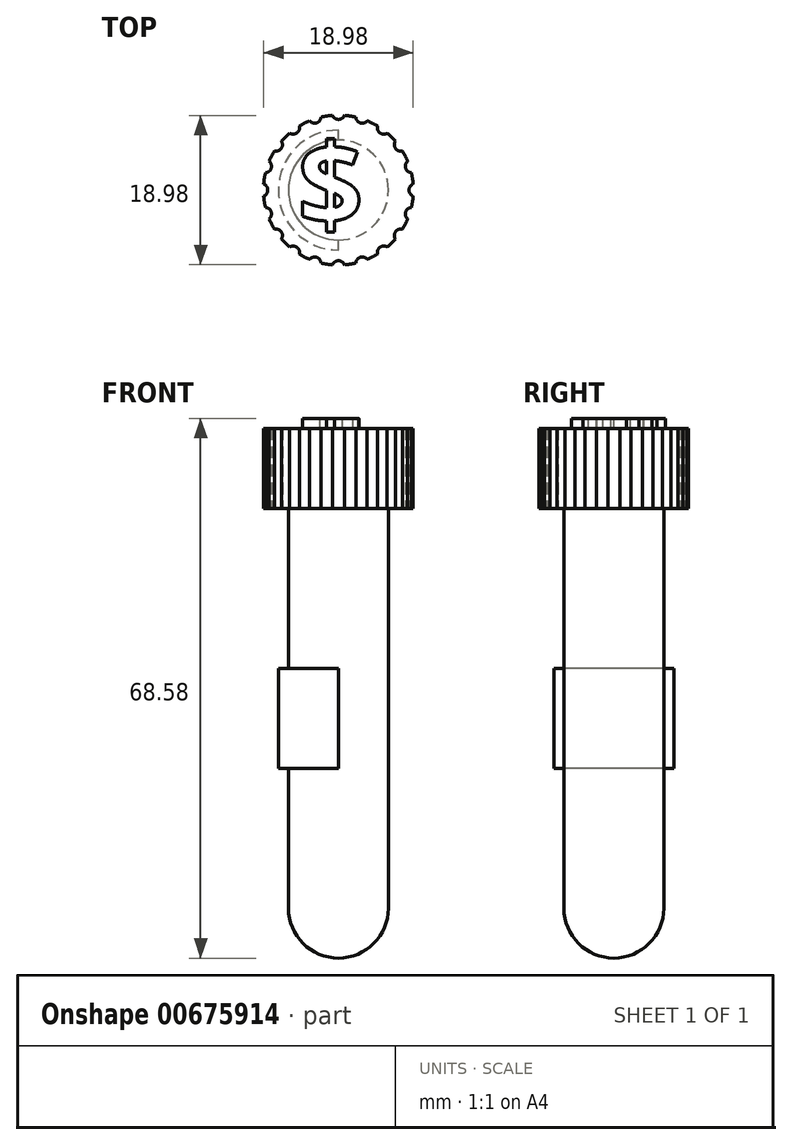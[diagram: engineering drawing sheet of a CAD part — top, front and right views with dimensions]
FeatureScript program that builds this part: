
annotation { "Feature Type Name" : "Feature", "Feature Type Description" : "" }
export const myFeature = defineFeature(function(context is Context, id is Id, definition is map)
    precondition{}
    {
        {
            var Q0;
            Q0=qCreatedBy(makeId("Top.planeOp"),FACE);
            var sketch = newSketch(context, id + "F0", { "sketchPlane" : qUnion([Q0])});
            skCircle(sketch, "E0", {"center": v(0, 0) * mm, "radius": 6.35 * mm});
            skSolve(sketch);
        }
        {
            var Q0;
            Q0 = qSketchRegion(id + "F0", true);
            extrude(context, id + "F1", {"entities" : qUnion([Q0]), "oppositeDirection" : true, "depth" : 50.8 * mm, "offsetDistance" : 25.4 * mm});
        }
        {
            var Q0;
            Q0=makeQuery(id+"F1.opExtrude","CAP_FACE",FACE,{"disambiguationData":[OSD([sQuery(id+"F0.wireOp",EDGE,"E0")])],"isStart":false});
            var sketch = newSketch(context, id + "F2", { "sketchPlane" : qUnion([Q0])});
            skArc(sketch, "E1", {"start": v(0, -6.35) * mm, "mid": v(6.35, 0) * mm, "end": v(0, 6.35) * mm});
            skLineSegment(sketch, "E2", {"start": v(0, 6.35) * mm, "end": v(0, -6.35) * mm});
            skSolve(sketch);
        }
        {
            var Q0;
            Q0 = qSketchRegion(id + "F2", true);
            var Q1;
            Q1=sQuery(id+"F2.wireOp",EDGE,"E2");
            revolve(context, id + "F3", {"operationType" : NewBodyOperationType.ADD, "entities" : qUnion([Q0]), "axis" : qUnion([Q1]), "revolveType" : RevolveType.FULL});
        }
        {
            var Q0;
            Q0=makeQuery(id+"F1.opExtrude","CAP_FACE",FACE,{"disambiguationData":[OSD([sQuery(id+"F0.wireOp",EDGE,"E0")])],"isStart":true});
            var sketch = newSketch(context, id + "F4", { "sketchPlane" : qUnion([Q0])});
            skCircle(sketch, "E3", {"center": v(0, 0) * mm, "radius": 9.53 * mm});
            skPoint(sketch, "E4", {"position": v(0, 9.53) * mm});
            skArc(sketch, "E5", {"start": v(-0.76, 9.5) * mm, "mid": v(0, 8.98) * mm, "end": v(0.76, 9.5) * mm});
            skArc(sketch, "E6.1.0", {"start": v(-3.66, 8.8) * mm, "mid": v(-2.77, 8.54) * mm, "end": v(-2.2, 9.27) * mm});
            skArc(sketch, "E6.2.0", {"start": v(-6.2, 7.23) * mm, "mid": v(-5.28, 7.26) * mm, "end": v(-4.96, 8.13) * mm});
            skArc(sketch, "E6.3.0", {"start": v(-8.13, 4.96) * mm, "mid": v(-7.26, 5.28) * mm, "end": v(-7.23, 6.2) * mm});
            skArc(sketch, "E6.4.0", {"start": v(-9.27, 2.2) * mm, "mid": v(-8.54, 2.77) * mm, "end": v(-8.8, 3.66) * mm});
            skArc(sketch, "E6.5.0", {"start": v(-9.5, -0.76) * mm, "mid": v(-8.98, 0) * mm, "end": v(-9.5, 0.76) * mm});
            skArc(sketch, "E6.6.0", {"start": v(-8.8, -3.66) * mm, "mid": v(-8.54, -2.77) * mm, "end": v(-9.27, -2.2) * mm});
            skArc(sketch, "E6.7.0", {"start": v(-7.23, -6.2) * mm, "mid": v(-7.26, -5.28) * mm, "end": v(-8.13, -4.96) * mm});
            skArc(sketch, "E6.8.0", {"start": v(-4.96, -8.13) * mm, "mid": v(-5.28, -7.26) * mm, "end": v(-6.2, -7.23) * mm});
            skArc(sketch, "E6.9.0", {"start": v(-2.2, -9.27) * mm, "mid": v(-2.77, -8.54) * mm, "end": v(-3.66, -8.8) * mm});
            skArc(sketch, "E6.10.0", {"start": v(0.76, -9.5) * mm, "mid": v(0, -8.98) * mm, "end": v(-0.76, -9.5) * mm});
            skArc(sketch, "E6.11.0", {"start": v(3.66, -8.8) * mm, "mid": v(2.77, -8.54) * mm, "end": v(2.2, -9.27) * mm});
            skArc(sketch, "E6.12.0", {"start": v(6.2, -7.23) * mm, "mid": v(5.28, -7.26) * mm, "end": v(4.96, -8.13) * mm});
            skArc(sketch, "E6.13.0", {"start": v(8.13, -4.96) * mm, "mid": v(7.26, -5.28) * mm, "end": v(7.23, -6.2) * mm});
            skArc(sketch, "E6.14.0", {"start": v(9.27, -2.2) * mm, "mid": v(8.54, -2.77) * mm, "end": v(8.8, -3.66) * mm});
            skArc(sketch, "E6.15.0", {"start": v(9.5, 0.76) * mm, "mid": v(8.98, 0) * mm, "end": v(9.5, -0.76) * mm});
            skArc(sketch, "E6.16.0", {"start": v(8.8, 3.66) * mm, "mid": v(8.54, 2.77) * mm, "end": v(9.27, 2.2) * mm});
            skArc(sketch, "E6.17.0", {"start": v(7.23, 6.2) * mm, "mid": v(7.26, 5.28) * mm, "end": v(8.13, 4.96) * mm});
            skArc(sketch, "E6.18.0", {"start": v(4.96, 8.13) * mm, "mid": v(5.28, 7.26) * mm, "end": v(6.2, 7.23) * mm});
            skArc(sketch, "E6.19.0", {"start": v(2.2, 9.27) * mm, "mid": v(2.77, 8.54) * mm, "end": v(3.66, 8.8) * mm});
            skSolve(sketch);
        }
        {
            var Q0;
            {var subQ0=sQuery(id+"F4.wireOp",EDGE,"E5");Q0=makeQuery(id+"F4.imprint","IMPRINT",FACE,{"disambiguationData":[TD([[makeQuery(id+"F4.imprint","IMPRINT",EDGE,{"derivedFrom":subQ0}),-1.0]])]});}
            var Q1;
            Q1=makeQuery(id+"F4.imprint","IMPRINT",FACE,{"disambiguationData":[TD([[makeQuery(id+"F4.imprint","IMPRINT",EDGE,{"derivedFrom":makeQuery(id+"F1.opExtrude","CAP_EDGE",EDGE,{"disambiguationData":[OSD([sQuery(id+"F0.wireOp",EDGE,"E0")])],"isStart":true})}),-1.0]])]});
            var Q2;
            Q2=makeQuery(id+"F4.imprint","IMPRINT",FACE,{"disambiguationData":[TD([[makeQuery(id+"F4.imprint","IMPRINT",EDGE,{"derivedFrom":makeQuery(id+"F1.opExtrude","CAP_EDGE",EDGE,{"disambiguationData":[OSD([sQuery(id+"F0.wireOp",EDGE,"E0")])],"isStart":true})}),1.0]])]});
            extrude(context, id + "F5", {"entities" : qUnion([Q0, Q1, Q2]), "depth" : 10.16 * mm, "offsetDistance" : 25.4 * mm});
        }
        {
            var Q0;
            Q0=qCreatedBy(makeId("Top.planeOp"),FACE);
            cPlane(context, id + "F6", {"entities" : qUnion([Q0]), "cplaneType" : CPlaneType.OFFSET, "offset" : 20.32 * mm, "oppositeDirection" : true, "width" : 152.4 * mm, "height" : 152.4 * mm});
        }
        {
            var Q0;
            Q0=qCreatedBy(id+"F6.planeOp",FACE);
            var sketch = newSketch(context, id + "F7", { "sketchPlane" : qUnion([Q0])});
            skArc(sketch, "E7", {"start": v(0, 7.62) * mm, "mid": v(-7.62, 0) * mm, "end": v(0, -7.62) * mm});
            skLineSegment(sketch, "E8", {"start": v(0, -7.62) * mm, "end": v(0, 7.62) * mm});
            skSolve(sketch);
        }
        {
            var Q0;
            Q0 = qSketchRegion(id + "F7", true);
            extrude(context, id + "F8", {"entities" : qUnion([Q0]), "operationType" : NewBodyOperationType.ADD, "oppositeDirection" : true, "depth" : 12.7 * mm, "offsetDistance" : 25.4 * mm});
        }
        {
            var Q0;
            Q0=makeQuery(id+"F5.opExtrude","CAP_FACE",FACE,{"disambiguationData":[OSD([sQuery(id+"F4.wireOp",EDGE,"E3"),sQuery(id+"F4.wireOp",EDGE,"E5"),sQuery(id+"F4.wireOp",EDGE,"E6.1.0"),sQuery(id+"F4.wireOp",EDGE,"E6.2.0"),sQuery(id+"F4.wireOp",EDGE,"E6.3.0"),sQuery(id+"F4.wireOp",EDGE,"E6.4.0"),sQuery(id+"F4.wireOp",EDGE,"E6.5.0"),sQuery(id+"F4.wireOp",EDGE,"E6.6.0"),sQuery(id+"F4.wireOp",EDGE,"E6.7.0"),sQuery(id+"F4.wireOp",EDGE,"E6.8.0"),sQuery(id+"F4.wireOp",EDGE,"E6.9.0"),sQuery(id+"F4.wireOp",EDGE,"E6.10.0"),sQuery(id+"F4.wireOp",EDGE,"E6.11.0"),sQuery(id+"F4.wireOp",EDGE,"E6.12.0"),sQuery(id+"F4.wireOp",EDGE,"E6.13.0"),sQuery(id+"F4.wireOp",EDGE,"E6.14.0"),sQuery(id+"F4.wireOp",EDGE,"E6.15.0"),sQuery(id+"F4.wireOp",EDGE,"E6.16.0"),sQuery(id+"F4.wireOp",EDGE,"E6.17.0"),sQuery(id+"F4.wireOp",EDGE,"E6.18.0"),sQuery(id+"F4.wireOp",EDGE,"E6.19.0")])],"isStart":false});
            var sketch = newSketch(context, id + "F9", { "sketchPlane" : qUnion([Q0])});
            skText(sketch, "E9", { "text": "$", "fontName": "OpenSans-Bold.ttf"});
            const initialGuessF9  = {"E9": [-0.00517, -0.0045, 1, 0, 0.0105]};
            skSetInitialGuess(sketch, initialGuessF9);
            skSolve(sketch);
        }
        {
            var Q0;
            Q0 = qSketchRegion(id + "F9", true);
            extrude(context, id + "F10", {"entities" : qUnion([Q0]), "operationType" : NewBodyOperationType.ADD, "depth" : 1.27 * mm, "offsetDistance" : 25.4 * mm});
        }
    });
